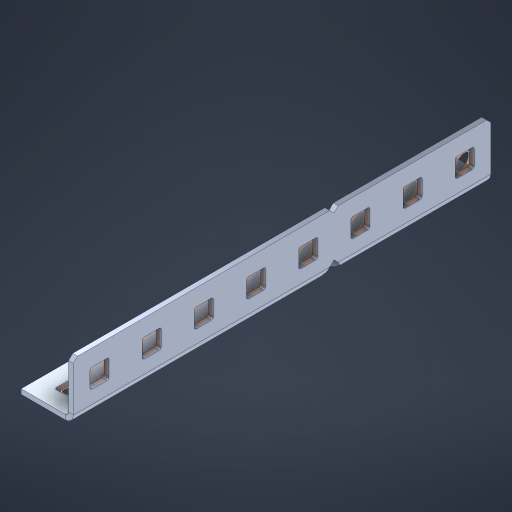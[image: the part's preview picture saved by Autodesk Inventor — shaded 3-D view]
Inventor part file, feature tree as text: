
AUTODESK INVENTOR PART (.ipt)
format: ipt  version: 2023 (Build 270158000, 158)  size: 509,440 bytes
history: native  units: in
note: dims shown in document units (in); Inventor stores cm internally (conversion verified against a paired STEP export)
features: other x21, extrude x15, sheet_metal_op x10, sketch x8, mirror x1, pattern_linear x1, chamfer x1
ambient origin geometry x8: Origin, YZ Plane, XZ Plane, XY Plane, X Axis, Y Axis, Z Axis, Center Point
bodies: Solid1 (feature_tree), Body (feature_tree)
feature tree (57):
  other  "Flange Pattern Plane"
  sheet_metal_op  "Flange Pattern"
  sheet_metal_op  "Body Pattern"
  other  "Arc Length"
  mirror  "Notch Mirror"
  pattern_linear  "Notch Pattern"  Spacing1=0.1875in  [1 undecoded]
  chamfer  "End Chamfer"
  extrude  "Half Cut"  Depth=0.0469in
  sketch  "Sketch1"  dims[d0=2.5in]
  other  "Plate1"
  sketch  "Sketch2"  dims[d1=4.0in]
  other  "Plate2"
  sheet_metal_op  "Bend1"
  sheet_metal_op  "Corner1"
  sketch  "Sketch3"  dims[d2=0.0469in]
  other  "Flange Pattern Sketch"
  sketch  "Sketch7"  dims[d3=0.0469in]
  other  "Srf1"
  other  "Srf2"
  sketch  "Sketch8"  dims[d4=0.0234in]
  sketch  "Sketch9"  dims[d5=0.0938in]
  other  "Srf91"
  sheet_metal_op  "Body Pattern Sketch"
  other  "Srf92"
  sketch  "Sketch13"  dims[d6=0.0469in]
  sketch  "Sketch14"  dims[d7=0.5in d8=90.0deg d9=0.0312in d10=0.1875in d11=0.0469in d12=0.0469in d16=0.182in d17=0.02in d18=0.0469in d19=0.0in d20=0.25in d21=0.25in d46=0.172in d47=1.0in d48=0.0in d49=0.182in d50=0.02in d51=0.25in d52=0.25in d53=0.0469in d54=0.0in d55=0.172in d56=1.0in d57=0.0in d60=3.1496in d62=0.5in d63=0.3937in d65=0.5in d85=0.1227in d86=0.1659in d88=0.04in d89=0.0469in d90=0.0in d91=0.04in d92=0.0491in d95=2.5in d96=0.04in d97=0.25in d98=45.0deg d101=0.0in d102=2.497in d131=0.5in d132=3.1496in d134=0.5in d139=0.5in]
  other  "Srf856"
  other  "Srf1310"
  other  "Srf1311"
  other  "Srf1312"
  other  "Srf1376"
  other  "Srf1377"
  other  "Srf1728"
  other  "Srf1755"
  other  "Srf1878"
  other  "Srf1879"
  other  "Srf1942"
  other  "Srf1943"
  sheet_metal_op  "Flange Stamp"
  sheet_metal_op  "Flange Circle"
  sheet_metal_op  "Body Stamp"
  sheet_metal_op  "Body Circle"
  sheet_metal_op  "Notch"
  extrude  "ExtrusionSrf2"  Depth=0.0469in
  extrude  "ExtrusionSrf92"  Depth=0.5in
  extrude  "ExtrusionSrf856"  Depth=0.02in
  extrude  "ExtrusionSrf1310"  Depth=0.0469in
  extrude  "ExtrusionSrf1311"  TaperAngle=0.0deg  [1 undecoded]
  extrude  "ExtrusionSrf1312"  Depth=0.5in
  extrude  "ExtrusionSrf1376"  Depth=0.5in
  extrude  "ExtrusionSrf1377"  Depth=0.5in
  extrude  "ExtrusionSrf1728"  Depth=0.5in TaperAngle=0.0deg
  extrude  "ExtrusionSrf1755"  Depth=0.5in
  extrude  "ExtrusionSrf1878"  Depth=0.02in
  extrude  "ExtrusionSrf1879"  Depth=0.5in
  extrude  "ExtrusionSrf1942"  Depth=0.5in
  extrude  "ExtrusionSrf1943"  Depth=0.0469in
note: 2 required parameter values undecoded (feature->parameter linkage not recoverable at this tier; creation-order binding heuristic only, values carry confidence <= 0.55)
